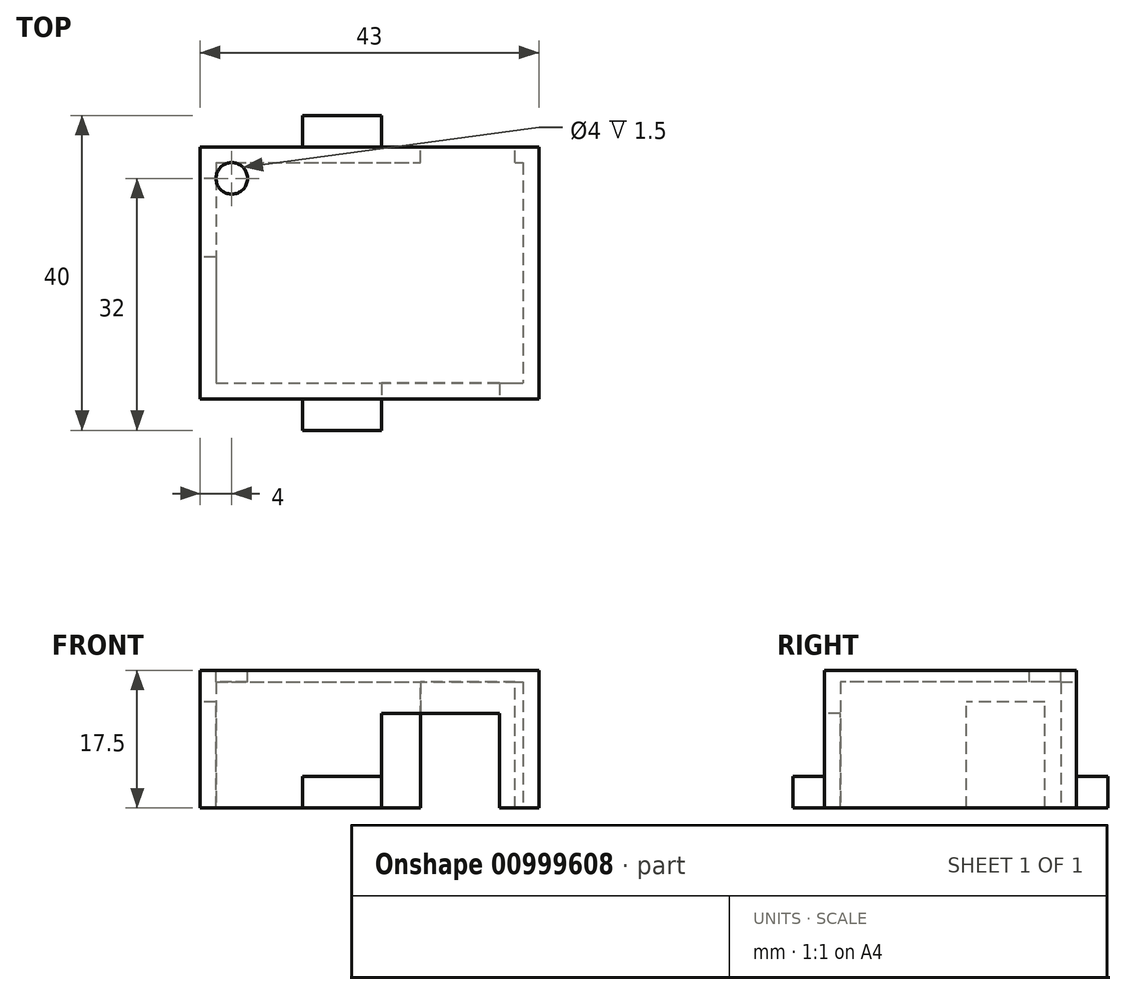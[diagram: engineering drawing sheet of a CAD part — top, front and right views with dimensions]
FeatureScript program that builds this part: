
annotation { "Feature Type Name" : "Feature", "Feature Type Description" : "" }
export const myFeature = defineFeature(function(context is Context, id is Id, definition is map)
    precondition{}
    {
        {
            var Q0;
            Q0=qCreatedBy(makeId("Top.planeOp"),FACE);
            var sketch = newSketch(context, id + "F0", { "sketchPlane" : qUnion([Q0])});
            skLineSegment(sketch, "E0.bottom", {"start": v(0, 0) * mm, "end": v(39, 0) * mm});
            skLineSegment(sketch, "E0.top", {"start": v(0, -28) * mm, "end": v(39, -28) * mm});
            skLineSegment(sketch, "E0.left", {"start": v(0, 0) * mm, "end": v(0, -28) * mm});
            skLineSegment(sketch, "E0.right", {"start": v(39, 0) * mm, "end": v(39, -28) * mm});
            skLineSegment(sketch, "E1.bottom", {"start": v(-2, 2) * mm, "end": v(41, 2) * mm});
            skLineSegment(sketch, "E1.top", {"start": v(-2, -30) * mm, "end": v(41, -30) * mm});
            skLineSegment(sketch, "E1.left", {"start": v(-2, 2) * mm, "end": v(-2, -30) * mm});
            skLineSegment(sketch, "E1.right", {"start": v(41, 2) * mm, "end": v(41, -30) * mm});
            skSolve(sketch);
        }
        {
            var Q0;
            Q0 = qSketchRegion(id + "F0", true);
            extrude(context, id + "F1", {"entities" : qUnion([Q0]), "depth" : 16 * mm, "offsetDistance" : 25 * mm});
        }
        {
            var Q0;
            Q0=makeQuery(id+"F1.opExtrude","CAP_FACE",FACE,{"disambiguationData":[OSD([sQuery(id+"F0.wireOp",EDGE,"E0.bottom"),sQuery(id+"F0.wireOp",EDGE,"E0.top"),sQuery(id+"F0.wireOp",EDGE,"E0.left"),sQuery(id+"F0.wireOp",EDGE,"E0.right"),sQuery(id+"F0.wireOp",EDGE,"E1.bottom"),sQuery(id+"F0.wireOp",EDGE,"E1.top"),sQuery(id+"F0.wireOp",EDGE,"E1.left"),sQuery(id+"F0.wireOp",EDGE,"E1.right")])],"isStart":false});
            var sketch = newSketch(context, id + "F2", { "sketchPlane" : qUnion([Q0])});
            skLineSegment(sketch, "E2.bottom", {"start": v(-2, 2) * mm, "end": v(41, 2) * mm});
            skLineSegment(sketch, "E2.top", {"start": v(-2, -30) * mm, "end": v(41, -30) * mm});
            skLineSegment(sketch, "E2.left", {"start": v(-2, 2) * mm, "end": v(-2, -30) * mm});
            skLineSegment(sketch, "E2.right", {"start": v(41, 2) * mm, "end": v(41, -30) * mm});
            skSolve(sketch);
        }
        {
            var Q0;
            Q0 = qSketchRegion(id + "F2", true);
            extrude(context, id + "F3", {"entities" : qUnion([Q0]), "operationType" : NewBodyOperationType.ADD, "depth" : 1.5 * mm, "offsetDistance" : 25 * mm});
        }
        {
            var Q0;
            Q0=makeQuery(id+"F3.boolean.opBoolean","MERGE",FACE,{"derivedFrom":[makeQuery(id+"F1.opExtrude","SWEPT_FACE",FACE,{"disambiguationData":[OSD([sQuery(id+"F0.wireOp",EDGE,"E1.left")])]}),makeQuery(id+"F3.opExtrude","SWEPT_FACE",FACE,{"disambiguationData":[OSD([sQuery(id+"F2.wireOp",EDGE,"E2.left")])]})]});
            var sketch = newSketch(context, id + "F4", { "sketchPlane" : qUnion([Q0])});
            skLineSegment(sketch, "E3.bottom", {"start": v(2, 0) * mm, "end": v(12, 0) * mm});
            skLineSegment(sketch, "E3.top", {"start": v(2, 13.5) * mm, "end": v(12, 13.5) * mm});
            skLineSegment(sketch, "E3.left", {"start": v(2, 0) * mm, "end": v(2, 13.5) * mm});
            skLineSegment(sketch, "E3.right", {"start": v(12, 0) * mm, "end": v(12, 13.5) * mm});
            skSolve(sketch);
        }
        {
            var Q0;
            Q0 = qSketchRegion(id + "F4", true);
            extrude(context, id + "F5", {"entities" : qUnion([Q0]), "operationType" : NewBodyOperationType.REMOVE, "endBound" : BoundingType.UP_TO_NEXT, "oppositeDirection" : true, "depth" : 25 * mm, "offsetDistance" : 25 * mm});
        }
        {
            var Q0;
            Q0=makeQuery(id+"F3.opExtrude","CAP_FACE",FACE,{"disambiguationData":[OSD([sQuery(id+"F2.wireOp",EDGE,"E2.bottom"),sQuery(id+"F2.wireOp",EDGE,"E2.top"),sQuery(id+"F2.wireOp",EDGE,"E2.left"),sQuery(id+"F2.wireOp",EDGE,"E2.right")])],"isStart":false});
            var sketch = newSketch(context, id + "F6", { "sketchPlane" : qUnion([Q0])});
            skCircle(sketch, "E4", {"center": v(2, -2) * mm, "radius": 2 * mm});
            skSolve(sketch);
        }
        {
            var Q0;
            Q0=makeQuery(id+"F6.imprint","IMPRINT",FACE,{"disambiguationData":[TD([[makeQuery(id+"F6.imprint","IMPRINT",EDGE,{"derivedFrom":sQuery(id+"F6.wireOp",EDGE,"E4")}),1.0]])]});
            var Q1;
            Q1=makeQuery(id+"F3.opExtrude","CAP_FACE",FACE,{"disambiguationData":[OSD([sQuery(id+"F2.wireOp",EDGE,"E2.bottom"),sQuery(id+"F2.wireOp",EDGE,"E2.top"),sQuery(id+"F2.wireOp",EDGE,"E2.left"),sQuery(id+"F2.wireOp",EDGE,"E2.right")])],"isStart":true});
            extrude(context, id + "F7", {"entities" : qUnion([Q0]), "operationType" : NewBodyOperationType.REMOVE, "endBound" : BoundingType.UP_TO_SURFACE, "oppositeDirection" : true, "depth" : 25 * mm, "endBoundEntityFace" : qUnion([Q1]), "offsetDistance" : 25 * mm});
        }
        {
            var Q0;
            Q0=makeQuery(id+"F3.boolean.opBoolean","MERGE",FACE,{"derivedFrom":[makeQuery(id+"F1.opExtrude","SWEPT_FACE",FACE,{"disambiguationData":[OSD([sQuery(id+"F0.wireOp",EDGE,"E1.bottom")])]}),makeQuery(id+"F3.opExtrude","SWEPT_FACE",FACE,{"disambiguationData":[OSD([sQuery(id+"F2.wireOp",EDGE,"E2.bottom")])]})]});
            var sketch = newSketch(context, id + "F8", { "sketchPlane" : qUnion([Q0])});
            skLineSegment(sketch, "E5.bottom", {"start": v(-38, 0) * mm, "end": v(-26, 0) * mm});
            skLineSegment(sketch, "E5.top", {"start": v(-38, 16) * mm, "end": v(-26, 16) * mm});
            skLineSegment(sketch, "E5.left", {"start": v(-38, 0) * mm, "end": v(-38, 16) * mm});
            skLineSegment(sketch, "E5.right", {"start": v(-26, 0) * mm, "end": v(-26, 16) * mm});
            skSolve(sketch);
        }
        {
            var Q0;
            Q0 = qSketchRegion(id + "F8", true);
            extrude(context, id + "F9", {"entities" : qUnion([Q0]), "operationType" : NewBodyOperationType.REMOVE, "endBound" : BoundingType.UP_TO_NEXT, "oppositeDirection" : true, "depth" : 25 * mm, "offsetDistance" : 25 * mm});
        }
        {
            var Q0;
            Q0=makeQuery(id+"F3.boolean.opBoolean","MERGE",FACE,{"derivedFrom":[makeQuery(id+"F1.opExtrude","SWEPT_FACE",FACE,{"disambiguationData":[OSD([sQuery(id+"F0.wireOp",EDGE,"E1.top")])]}),makeQuery(id+"F3.opExtrude","SWEPT_FACE",FACE,{"disambiguationData":[OSD([sQuery(id+"F2.wireOp",EDGE,"E2.top")])]})]});
            var sketch = newSketch(context, id + "F10", { "sketchPlane" : qUnion([Q0])});
            skLineSegment(sketch, "E6.bottom", {"start": v(36, 0) * mm, "end": v(21, 0) * mm});
            skLineSegment(sketch, "E6.top", {"start": v(36, 12) * mm, "end": v(21, 12) * mm});
            skLineSegment(sketch, "E6.left", {"start": v(36, 0) * mm, "end": v(36, 12) * mm});
            skLineSegment(sketch, "E6.right", {"start": v(21, 0) * mm, "end": v(21, 12) * mm});
            skSolve(sketch);
        }
        {
            var Q0;
            Q0 = qSketchRegion(id + "F10", true);
            extrude(context, id + "F11", {"entities" : qUnion([Q0]), "operationType" : NewBodyOperationType.REMOVE, "endBound" : BoundingType.UP_TO_NEXT, "oppositeDirection" : true, "depth" : 25 * mm, "offsetDistance" : 25 * mm});
        }
        {
            var Q0;
            Q0=makeQuery(id+"F3.boolean.opBoolean","MERGE",FACE,{"derivedFrom":[makeQuery(id+"F1.opExtrude","SWEPT_FACE",FACE,{"disambiguationData":[OSD([sQuery(id+"F0.wireOp",EDGE,"E1.top")])]}),makeQuery(id+"F3.opExtrude","SWEPT_FACE",FACE,{"disambiguationData":[OSD([sQuery(id+"F2.wireOp",EDGE,"E2.top")])]})]});
            var sketch = newSketch(context, id + "F12", { "sketchPlane" : qUnion([Q0])});
            skLineSegment(sketch, "E7.bottom", {"start": v(11, 0) * mm, "end": v(21, 0) * mm});
            skLineSegment(sketch, "E7.top", {"start": v(11, 4) * mm, "end": v(21, 4) * mm});
            skLineSegment(sketch, "E7.left", {"start": v(11, 0) * mm, "end": v(11, 4) * mm});
            skLineSegment(sketch, "E7.right", {"start": v(21, 0) * mm, "end": v(21, 4) * mm});
            skSolve(sketch);
        }
        {
            var Q0;
            Q0 = qSketchRegion(id + "F12", true);
            extrude(context, id + "F13", {"entities" : qUnion([Q0]), "operationType" : NewBodyOperationType.ADD, "depth" : 4 * mm, "offsetDistance" : 25 * mm});
        }
        {
            var Q0;
            Q0=makeQuery(id+"F3.boolean.opBoolean","MERGE",FACE,{"derivedFrom":[makeQuery(id+"F1.opExtrude","SWEPT_FACE",FACE,{"disambiguationData":[OSD([sQuery(id+"F0.wireOp",EDGE,"E1.bottom")])]}),makeQuery(id+"F3.opExtrude","SWEPT_FACE",FACE,{"disambiguationData":[OSD([sQuery(id+"F2.wireOp",EDGE,"E2.bottom")])]})]});
            var sketch = newSketch(context, id + "F14", { "sketchPlane" : qUnion([Q0])});
            skLineSegment(sketch, "E8.bottom", {"start": v(-11, 0) * mm, "end": v(-21, 0) * mm});
            skLineSegment(sketch, "E8.top", {"start": v(-11, 4) * mm, "end": v(-21, 4) * mm});
            skLineSegment(sketch, "E8.left", {"start": v(-11, 0) * mm, "end": v(-11, 4) * mm});
            skLineSegment(sketch, "E8.right", {"start": v(-21, 0) * mm, "end": v(-21, 4) * mm});
            skSolve(sketch);
        }
        {
            var Q0;
            Q0 = qSketchRegion(id + "F14", true);
            extrude(context, id + "F15", {"entities" : qUnion([Q0]), "operationType" : NewBodyOperationType.ADD, "depth" : 4 * mm, "offsetDistance" : 25 * mm});
        }
    });
